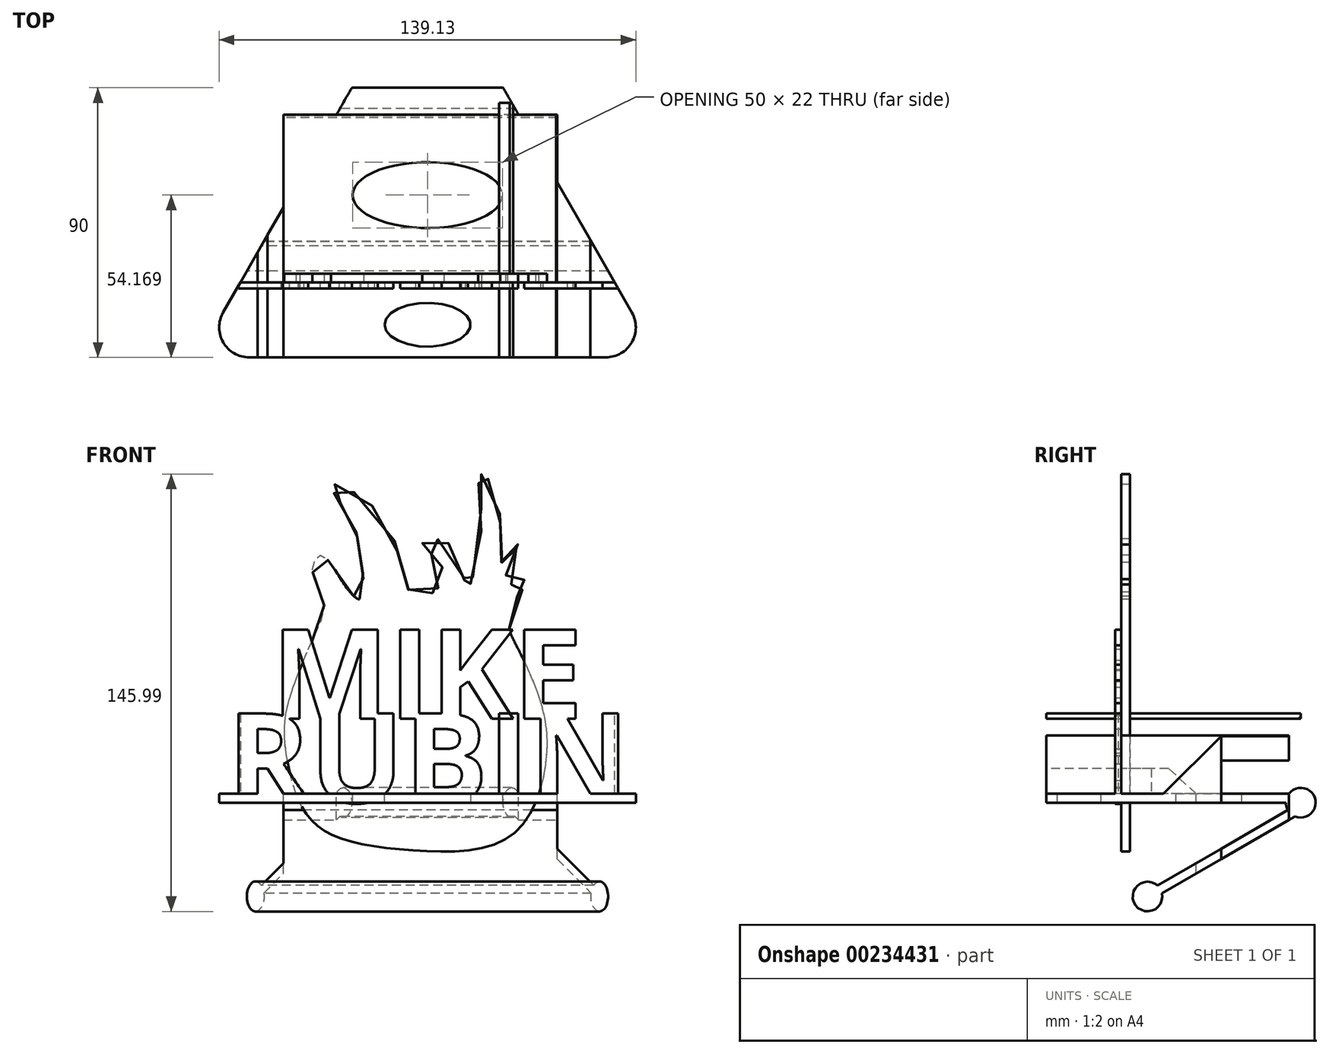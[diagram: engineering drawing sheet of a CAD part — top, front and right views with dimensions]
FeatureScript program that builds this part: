
annotation { "Feature Type Name" : "Feature", "Feature Type Description" : "" }
export const myFeature = defineFeature(function(context is Context, id is Id, definition is map)
    precondition{}
    {
        {
            var Q0;
            Q0=qCreatedBy(makeId("Front.planeOp"),FACE);
            var sketch = newSketch(context, id + "F0", { "sketchPlane" : qUnion([Q0])});
            skText(sketch, "E0", { "text": "MIKE", "fontName": "OpenSans-Bold.ttf"});
            skText(sketch, "E1", { "text": "RUBIN", "fontName": "OpenSans-Bold.ttf"});
            skLineSegment(sketch, "E2.bottom", {"start": v(-73.25, -22.3) * mm, "end": v(80.38, -22.3) * mm});
            skLineSegment(sketch, "E2.top", {"start": v(-73.25, -19.3) * mm, "end": v(80.38, -19.3) * mm});
            skLineSegment(sketch, "E2.left", {"start": v(-73.25, -22.3) * mm, "end": v(-73.25, -19.3) * mm});
            skLineSegment(sketch, "E2.right", {"start": v(80.38, -22.3) * mm, "end": v(80.38, -19.3) * mm});
            const initialGuessF0  = {"E0": [-0.0486, 0.00568, 1, 0, 0.03], "E1": [-0.06325, -0.0223, 1, 0, 0.03]};
            skSetInitialGuess(sketch, initialGuessF0);
            skSolve(sketch);
        }
        {
            var Q0;
            Q0=qCreatedBy(makeId("Front.planeOp"),FACE);
            var sketch = newSketch(context, id + "F1", { "sketchPlane" : qUnion([Q0])});
            skFitSpline(sketch, "E3", {"points": [v(0, -38.3) * mm, v(-27.15, -33.53) * mm, v(-37.73, -24.83) * mm, v(-43.2, -8.44) * mm, v(-44.05, 5.04) * mm, v(-40.46, 18.52) * mm, v(-33.64, 34.74) * mm, v(-31.08, 44.8) * mm, v(-34.83, 54.7) * mm, v(-32.1, 60.34) * mm, v(-23.57, 49.59) * mm, v(-18.62, 45.83) * mm, v(-18.45, 58.46) * mm, v(-22.89, 73.82) * mm, v(-28.52, 83.72) * mm, v(-10.94, 72.45) * mm, v(-2.92, 48.9) * mm, v(4.6, 47.37) * mm, v(8.69, 55.9) * mm, v(1.86, 64.77) * mm, v(12.78, 62.56) * mm, v(16.37, 48.05) * mm, v(21.66, 71.09) * mm, v(20.98, 87.3) * mm, v(27.12, 79.11) * mm, v(28.66, 57.95) * mm, v(33.78, 63.92) * mm, v(29.85, 50.95) * mm, v(37.02, 52.32) * mm, v(31.05, 41.9) * mm, v(33.1, 30.47) * mm, v(41.12, 11.87) * mm, v(43.16, -7.59) * mm, v(32.07, -32.85) * mm, v(0, -38.3) * mm]});
            skSolve(sketch);
        }
        {
            var Q0;
            {var subQ5=sQuery(id+"F0.wireOp",EDGE,"E0.sketch_text.stroke-0");Q0=makeQuery(id+"F0.imprint","IMPRINT",FACE,{"disambiguationData":[TD([[makeQuery(id+"F0.imprint","IMPRINT",EDGE,{"derivedFrom":subQ5}),-1.0]])]});}
            var Q1;
            {var subQ1=sQuery(id+"F0.wireOp",EDGE,"E0.sketch_text.stroke-19");Q1=makeQuery(id+"F0.imprint","IMPRINT",FACE,{"disambiguationData":[TD([[makeQuery(id+"F0.imprint","IMPRINT",EDGE,{"derivedFrom":subQ1}),-1.0]])]});}
            var Q2;
            {var subQ8=sQuery(id+"F0.wireOp",EDGE,"E0.sketch_text.stroke-24");Q2=makeQuery(id+"F0.imprint","IMPRINT",FACE,{"disambiguationData":[TD([[makeQuery(id+"F0.imprint","IMPRINT",EDGE,{"derivedFrom":subQ8}),-1.0]])]});}
            var Q3;
            {var subQ4=sQuery(id+"F0.wireOp",EDGE,"E0.sketch_text.stroke-37");Q3=makeQuery(id+"F0.imprint","IMPRINT",FACE,{"disambiguationData":[TD([[makeQuery(id+"F0.imprint","IMPRINT",EDGE,{"derivedFrom":subQ4}),-1.0]])]});}
            var Q4;
            {var subQ0=sQuery(id+"F0.wireOp",EDGE,"E0.sketch_text.stroke-35");var subQ1=sQuery(id+"F0.wireOp",EDGE,"E0.sketch_text.stroke-23");var subQ2=makeQuery(id+"F0.imprint","INTERSECT",VERTEX,{"derivedFrom":[subQ1,subQ0]});Q4=makeQuery(id+"F0.imprint","IMPRINT",FACE,{"disambiguationData":[TD([[makeQuery(id+"F0.imprint","IMPRINT",EDGE,{"disambiguationData":[TD([[subQ2,-1.0]])],"derivedFrom":subQ1}),-1.0]])]});}
            var Q5;
            {var subQ5=sQuery(id+"F0.wireOp",EDGE,"E0.sketch_text.stroke-27");Q5=makeQuery(id+"F0.imprint","IMPRINT",FACE,{"disambiguationData":[TD([[makeQuery(id+"F0.imprint","IMPRINT",EDGE,{"derivedFrom":subQ5}),-1.0]])]});}
            var Q6;
            {var subQ5=sQuery(id+"F0.wireOp",EDGE,"E1.sketch_text.stroke-70");Q6=makeQuery(id+"F0.imprint","IMPRINT",FACE,{"disambiguationData":[TD([[makeQuery(id+"F0.imprint","IMPRINT",EDGE,{"derivedFrom":subQ5}),-1.0]])]});}
            var Q7;
            {var subQ15=sQuery(id+"F0.wireOp",EDGE,"E1.sketch_text.stroke-65");Q7=makeQuery(id+"F0.imprint","IMPRINT",FACE,{"disambiguationData":[TD([[makeQuery(id+"F0.imprint","IMPRINT",EDGE,{"derivedFrom":subQ15}),-1.0]])]});}
            var Q8;
            {var subQ3=sQuery(id+"F0.wireOp",EDGE,"E0.sketch_text.stroke-35");var subQ6=sQuery(id+"F0.wireOp",EDGE,"E0.sketch_text.stroke-23");var subQ10=makeQuery(id+"F0.imprint","INTERSECT",VERTEX,{"derivedFrom":[subQ6,subQ3]});Q8=makeQuery(id+"F0.imprint","IMPRINT",FACE,{"disambiguationData":[TD([[makeQuery(id+"F0.imprint","IMPRINT",EDGE,{"disambiguationData":[TD([[subQ10,-1.0]])],"derivedFrom":subQ6}),1.0]])]});}
            var Q9;
            {var subQ12=sQuery(id+"F0.wireOp",EDGE,"E0.sketch_text.stroke-27");Q9=makeQuery(id+"F0.imprint","IMPRINT",FACE,{"disambiguationData":[TD([[makeQuery(id+"F0.imprint","IMPRINT",EDGE,{"derivedFrom":subQ12}),1.0]])]});}
            var Q10;
            {var subQ23=sQuery(id+"F0.wireOp",EDGE,"E1.sketch_text.stroke-19");Q10=makeQuery(id+"F0.imprint","IMPRINT",FACE,{"disambiguationData":[TD([[makeQuery(id+"F0.imprint","IMPRINT",EDGE,{"derivedFrom":subQ23}),-1.0]])]});}
            var Q11;
            Q11=makeQuery(id+"F0.imprint","IMPRINT",FACE,{"disambiguationData":[TD([[makeQuery(id+"F0.imprint","IMPRINT",EDGE,{"derivedFrom":sQuery(id+"F0.wireOp",EDGE,"E1.sketch_text.stroke-0")}),-1.0]])]});
            var Q12;
            {var subQ7=sQuery(id+"F0.wireOp",EDGE,"E1.sketch_text.stroke-26");Q12=makeQuery(id+"F0.imprint","IMPRINT",FACE,{"disambiguationData":[TD([[makeQuery(id+"F0.imprint","IMPRINT",EDGE,{"derivedFrom":subQ7}),-1.0]])]});}
            var Q13;
            {var subQ0=sQuery(id+"F0.wireOp",EDGE,"E0.sketch_text.stroke-12");var subQ1=sQuery(id+"F0.wireOp",EDGE,"E0.sketch_text.stroke-11");var subQ2=makeQuery(id+"F0.imprint","INTERSECT",VERTEX,{"derivedFrom":[subQ1,subQ0]});Q13=makeQuery(id+"F0.imprint","IMPRINT",FACE,{"disambiguationData":[TD([[makeQuery(id+"F0.imprint","IMPRINT",EDGE,{"disambiguationData":[TD([[subQ2,1.0]])],"derivedFrom":subQ1}),-1.0]])]});}
            var Q14;
            {var subQ0=sQuery(id+"F0.wireOp",EDGE,"E0.sketch_text.stroke-5");var subQ1=sQuery(id+"F0.wireOp",EDGE,"E0.sketch_text.stroke-4");var subQ2=makeQuery(id+"F0.imprint","INTERSECT",VERTEX,{"derivedFrom":[subQ1,subQ0]});Q14=makeQuery(id+"F0.imprint","IMPRINT",FACE,{"disambiguationData":[TD([[makeQuery(id+"F0.imprint","IMPRINT",EDGE,{"disambiguationData":[TD([[subQ2,1.0]])],"derivedFrom":subQ1}),-1.0]])]});}
            var Q15;
            {var subQ0=sQuery(id+"F0.wireOp",EDGE,"E0.sketch_text.stroke-22");var subQ1=sQuery(id+"F0.wireOp",EDGE,"E0.sketch_text.stroke-21");var subQ2=makeQuery(id+"F0.imprint","INTERSECT",VERTEX,{"derivedFrom":[subQ1,subQ0]});Q15=makeQuery(id+"F0.imprint","IMPRINT",FACE,{"disambiguationData":[TD([[makeQuery(id+"F0.imprint","IMPRINT",EDGE,{"disambiguationData":[TD([[subQ2,1.0]])],"derivedFrom":subQ1}),-1.0]])]});}
            var Q16;
            {var subQ0=sQuery(id+"F0.wireOp",EDGE,"E2.bottom");var subQ1=sQuery(id+"F0.wireOp",EDGE,"E1.sketch_text.stroke-67");var subQ2=makeQuery(id+"F0.imprint","INTERSECT",VERTEX,{"derivedFrom":[subQ1,subQ0]});Q16=makeQuery(id+"F0.imprint","IMPRINT",FACE,{"disambiguationData":[TD([[makeQuery(id+"F0.imprint","IMPRINT",EDGE,{"disambiguationData":[TD([[subQ2,1.0]])],"derivedFrom":subQ1}),-1.0]])]});}
            var Q17;
            {var subQ0=sQuery(id+"F0.wireOp",EDGE,"E2.bottom");var subQ1=sQuery(id+"F0.wireOp",EDGE,"E1.sketch_text.stroke-64");var subQ2=makeQuery(id+"F0.imprint","INTERSECT",VERTEX,{"derivedFrom":[subQ1,subQ0]});Q17=makeQuery(id+"F0.imprint","IMPRINT",FACE,{"disambiguationData":[TD([[makeQuery(id+"F0.imprint","IMPRINT",EDGE,{"disambiguationData":[TD([[subQ2,-1.0]])],"derivedFrom":subQ1}),-1.0]])]});}
            var Q18;
            {var subQ0=sQuery(id+"F0.wireOp",EDGE,"E2.bottom");var subQ1=sQuery(id+"F0.wireOp",EDGE,"E1.sketch_text.stroke-59");var subQ2=makeQuery(id+"F0.imprint","INTERSECT",VERTEX,{"derivedFrom":[subQ1,subQ0]});Q18=makeQuery(id+"F0.imprint","IMPRINT",FACE,{"disambiguationData":[TD([[makeQuery(id+"F0.imprint","IMPRINT",EDGE,{"disambiguationData":[TD([[subQ2,-1.0]])],"derivedFrom":subQ1}),-1.0]])]});}
            var Q19;
            {var subQ1=sQuery(id+"F0.wireOp",EDGE,"E1.sketch_text.stroke-43");Q19=makeQuery(id+"F0.imprint","IMPRINT",FACE,{"disambiguationData":[TD([[makeQuery(id+"F0.imprint","IMPRINT",EDGE,{"derivedFrom":subQ1}),-1.0]])]});}
            var Q20;
            {var subQ7=sQuery(id+"F0.wireOp",EDGE,"E1.sketch_text.stroke-22");var subQ8=sQuery(id+"F0.wireOp",EDGE,"E1.sketch_text.stroke-21");var subQ9=makeQuery(id+"F0.imprint","INTERSECT",VERTEX,{"derivedFrom":[subQ8,subQ7]});Q20=makeQuery(id+"F0.imprint","IMPRINT",FACE,{"disambiguationData":[TD([[makeQuery(id+"F0.imprint","IMPRINT",EDGE,{"disambiguationData":[TD([[subQ9,1.0]])],"derivedFrom":subQ8}),-1.0]])]});}
            var Q21;
            {var subQ0=sQuery(id+"F0.wireOp",EDGE,"E2.bottom");var subQ1=sQuery(id+"F0.wireOp",EDGE,"E1.sketch_text.stroke-15");var subQ2=makeQuery(id+"F0.imprint","INTERSECT",VERTEX,{"derivedFrom":[subQ1,subQ0]});Q21=makeQuery(id+"F0.imprint","IMPRINT",FACE,{"disambiguationData":[TD([[makeQuery(id+"F0.imprint","IMPRINT",EDGE,{"disambiguationData":[TD([[subQ2,1.0]])],"derivedFrom":subQ1}),-1.0]])]});}
            var Q22;
            {var subQ0=sQuery(id+"F0.wireOp",EDGE,"E2.bottom");var subQ1=sQuery(id+"F0.wireOp",EDGE,"E1.sketch_text.stroke-7");var subQ2=makeQuery(id+"F0.imprint","INTERSECT",VERTEX,{"derivedFrom":[subQ1,subQ0]});Q22=makeQuery(id+"F0.imprint","IMPRINT",FACE,{"disambiguationData":[TD([[makeQuery(id+"F0.imprint","IMPRINT",EDGE,{"disambiguationData":[TD([[subQ2,1.0]])],"derivedFrom":subQ1}),-1.0]])]});}
            var Q23;
            {var subQ0=sQuery(id+"F0.wireOp",EDGE,"E1.sketch_text.stroke-23");var subQ1=sQuery(id+"F0.wireOp",EDGE,"E1.sketch_text.stroke-22");var subQ2=makeQuery(id+"F0.imprint","INTERSECT",VERTEX,{"derivedFrom":[subQ1,subQ0]});Q23=makeQuery(id+"F0.imprint","IMPRINT",FACE,{"disambiguationData":[TD([[makeQuery(id+"F0.imprint","IMPRINT",EDGE,{"disambiguationData":[TD([[subQ2,1.0]])],"derivedFrom":subQ1}),-1.0]])]});}
            extrude(context, id + "F2", {"entities" : qUnion([Q0, Q1, Q2, Q3, Q4, Q5, Q6, Q7, Q8, Q9, Q10, Q11, Q12, Q13, Q14, Q15, Q16, Q17, Q18, Q19, Q20, Q21, Q22, Q23]), "depth" : 2 * mm});
        }
        {
            var Q0;
            Q0=makeQuery(id+"F1.imprint","IMPRINT",FACE,{"disambiguationData":[TD([[makeQuery(id+"F1.imprint","IMPRINT",EDGE,{"derivedFrom":sQuery(id+"F1.wireOp",EDGE,"E3")}),-1.0]])]});
            extrude(context, id + "F3", {"entities" : qUnion([Q0]), "operationType" : NewBodyOperationType.ADD, "oppositeDirection" : true, "depth" : 3 * mm});
        }
        {
            var Q0;
            {var subQ5=sQuery(id+"F0.wireOp",EDGE,"E2.right");Q0=makeQuery(id+"F0.imprint","IMPRINT",FACE,{"disambiguationData":[TD([[makeQuery(id+"F0.imprint","IMPRINT",EDGE,{"derivedFrom":subQ5}),1.0]])]});}
            var Q1;
            {var subQ0=sQuery(id+"F0.wireOp",EDGE,"E2.bottom");var subQ1=sQuery(id+"F0.wireOp",EDGE,"E1.sketch_text.stroke-64");var subQ2=makeQuery(id+"F0.imprint","INTERSECT",VERTEX,{"derivedFrom":[subQ1,subQ0]});Q1=makeQuery(id+"F0.imprint","IMPRINT",FACE,{"disambiguationData":[TD([[makeQuery(id+"F0.imprint","IMPRINT",EDGE,{"disambiguationData":[TD([[subQ2,-1.0]])],"derivedFrom":subQ1}),-1.0]])]});}
            var Q2;
            {var subQ0=sQuery(id+"F0.wireOp",EDGE,"E2.bottom");var subQ1=sQuery(id+"F0.wireOp",EDGE,"E1.sketch_text.stroke-64");var subQ2=makeQuery(id+"F0.imprint","INTERSECT",VERTEX,{"derivedFrom":[subQ1,subQ0]});Q2=makeQuery(id+"F0.imprint","IMPRINT",FACE,{"disambiguationData":[TD([[makeQuery(id+"F0.imprint","IMPRINT",EDGE,{"disambiguationData":[TD([[subQ2,-1.0]])],"derivedFrom":subQ1}),1.0]])]});}
            var Q3;
            {var subQ0=sQuery(id+"F0.wireOp",EDGE,"E2.bottom");var subQ1=sQuery(id+"F0.wireOp",EDGE,"E1.sketch_text.stroke-67");var subQ2=makeQuery(id+"F0.imprint","INTERSECT",VERTEX,{"derivedFrom":[subQ1,subQ0]});Q3=makeQuery(id+"F0.imprint","IMPRINT",FACE,{"disambiguationData":[TD([[makeQuery(id+"F0.imprint","IMPRINT",EDGE,{"disambiguationData":[TD([[subQ2,1.0]])],"derivedFrom":subQ1}),-1.0]])]});}
            var Q4;
            {var subQ0=sQuery(id+"F0.wireOp",EDGE,"E2.bottom");var subQ1=sQuery(id+"F0.wireOp",EDGE,"E1.sketch_text.stroke-61");var subQ2=makeQuery(id+"F0.imprint","INTERSECT",VERTEX,{"derivedFrom":[subQ1,subQ0]});Q4=makeQuery(id+"F0.imprint","IMPRINT",FACE,{"disambiguationData":[TD([[makeQuery(id+"F0.imprint","IMPRINT",EDGE,{"disambiguationData":[TD([[subQ2,1.0]])],"derivedFrom":subQ1}),1.0]])]});}
            var Q5;
            {var subQ0=sQuery(id+"F0.wireOp",EDGE,"E2.bottom");var subQ1=sQuery(id+"F0.wireOp",EDGE,"E1.sketch_text.stroke-59");var subQ2=makeQuery(id+"F0.imprint","INTERSECT",VERTEX,{"derivedFrom":[subQ1,subQ0]});Q5=makeQuery(id+"F0.imprint","IMPRINT",FACE,{"disambiguationData":[TD([[makeQuery(id+"F0.imprint","IMPRINT",EDGE,{"disambiguationData":[TD([[subQ2,-1.0]])],"derivedFrom":subQ1}),-1.0]])]});}
            var Q6;
            {var subQ1=sQuery(id+"F0.wireOp",EDGE,"E1.sketch_text.stroke-43");Q6=makeQuery(id+"F0.imprint","IMPRINT",FACE,{"disambiguationData":[TD([[makeQuery(id+"F0.imprint","IMPRINT",EDGE,{"derivedFrom":subQ1}),1.0]])]});}
            var Q7;
            {var subQ1=sQuery(id+"F0.wireOp",EDGE,"E1.sketch_text.stroke-43");Q7=makeQuery(id+"F0.imprint","IMPRINT",FACE,{"disambiguationData":[TD([[makeQuery(id+"F0.imprint","IMPRINT",EDGE,{"derivedFrom":subQ1}),-1.0]])]});}
            var Q8;
            {var subQ3=sQuery(id+"F0.wireOp",EDGE,"E1.sketch_text.stroke-22");var subQ5=sQuery(id+"F0.wireOp",EDGE,"E1.sketch_text.stroke-21");var subQ6=makeQuery(id+"F0.imprint","INTERSECT",VERTEX,{"derivedFrom":[subQ5,subQ3]});Q8=makeQuery(id+"F0.imprint","IMPRINT",FACE,{"disambiguationData":[TD([[makeQuery(id+"F0.imprint","IMPRINT",EDGE,{"disambiguationData":[TD([[subQ6,1.0]])],"derivedFrom":subQ5}),1.0]])]});}
            var Q9;
            {var subQ5=sQuery(id+"F0.wireOp",EDGE,"E2.left");Q9=makeQuery(id+"F0.imprint","IMPRINT",FACE,{"disambiguationData":[TD([[makeQuery(id+"F0.imprint","IMPRINT",EDGE,{"derivedFrom":subQ5}),-1.0]])]});}
            var Q10;
            {var subQ0=sQuery(id+"F0.wireOp",EDGE,"E2.bottom");var subQ1=sQuery(id+"F0.wireOp",EDGE,"E1.sketch_text.stroke-7");var subQ2=makeQuery(id+"F0.imprint","INTERSECT",VERTEX,{"derivedFrom":[subQ1,subQ0]});Q10=makeQuery(id+"F0.imprint","IMPRINT",FACE,{"disambiguationData":[TD([[makeQuery(id+"F0.imprint","IMPRINT",EDGE,{"disambiguationData":[TD([[subQ2,1.0]])],"derivedFrom":subQ1}),-1.0]])]});}
            var Q11;
            {var subQ0=sQuery(id+"F0.wireOp",EDGE,"E2.bottom");var subQ1=sQuery(id+"F0.wireOp",EDGE,"E1.sketch_text.stroke-7");var subQ2=makeQuery(id+"F0.imprint","INTERSECT",VERTEX,{"derivedFrom":[subQ1,subQ0]});Q11=makeQuery(id+"F0.imprint","IMPRINT",FACE,{"disambiguationData":[TD([[makeQuery(id+"F0.imprint","IMPRINT",EDGE,{"disambiguationData":[TD([[subQ2,1.0]])],"derivedFrom":subQ1}),1.0]])]});}
            var Q12;
            {var subQ0=sQuery(id+"F0.wireOp",EDGE,"E2.bottom");var subQ1=sQuery(id+"F0.wireOp",EDGE,"E1.sketch_text.stroke-15");var subQ2=makeQuery(id+"F0.imprint","INTERSECT",VERTEX,{"derivedFrom":[subQ1,subQ0]});Q12=makeQuery(id+"F0.imprint","IMPRINT",FACE,{"disambiguationData":[TD([[makeQuery(id+"F0.imprint","IMPRINT",EDGE,{"disambiguationData":[TD([[subQ2,1.0]])],"derivedFrom":subQ1}),-1.0]])]});}
            var Q13;
            {var subQ0=sQuery(id+"F0.wireOp",EDGE,"E2.bottom");var subQ1=sQuery(id+"F0.wireOp",EDGE,"E1.sketch_text.stroke-15");var subQ2=makeQuery(id+"F0.imprint","INTERSECT",VERTEX,{"derivedFrom":[subQ1,subQ0]});Q13=makeQuery(id+"F0.imprint","IMPRINT",FACE,{"disambiguationData":[TD([[makeQuery(id+"F0.imprint","IMPRINT",EDGE,{"disambiguationData":[TD([[subQ2,1.0]])],"derivedFrom":subQ1}),1.0]])]});}
            var Q14;
            {var subQ7=sQuery(id+"F0.wireOp",EDGE,"E1.sketch_text.stroke-22");var subQ8=sQuery(id+"F0.wireOp",EDGE,"E1.sketch_text.stroke-21");var subQ9=makeQuery(id+"F0.imprint","INTERSECT",VERTEX,{"derivedFrom":[subQ8,subQ7]});Q14=makeQuery(id+"F0.imprint","IMPRINT",FACE,{"disambiguationData":[TD([[makeQuery(id+"F0.imprint","IMPRINT",EDGE,{"disambiguationData":[TD([[subQ9,1.0]])],"derivedFrom":subQ8}),-1.0]])]});}
            extrude(context, id + "F4", {"entities" : qUnion([Q0, Q1, Q2, Q3, Q4, Q5, Q6, Q7, Q8, Q9, Q10, Q11, Q12, Q13, Q14]), "operationType" : NewBodyOperationType.ADD, "oppositeDirection" : true, "depth" : 60 * mm, "hasSecondDirection" : true, "secondDirectionOppositeDirection" : false, "secondDirectionDepth" : 25 * mm});
        }
        {
            var Q0;
            Q0=makeQuery(id+"F4.opExtrude","SWEPT_FACE",FACE,{"disambiguationData":[OSD([sQuery(id+"F0.wireOp",EDGE,"E2.left")])]});
            var sketch = newSketch(context, id + "F5", { "sketchPlane" : qUnion([Q0])});
            skLineSegment(sketch, "E4", {"start": v(-60, -22.3) * mm, "end": v(-8.04, -52.3) * mm});
            skLineSegment(sketch, "E5", {"start": v(-60, -22.3) * mm, "end": v(-61.5, -24.9) * mm});
            skLineSegment(sketch, "E6", {"start": v(-61.5, -24.9) * mm, "end": v(-9.54, -54.9) * mm});
            skLineSegment(sketch, "E7", {"start": v(-9.54, -54.9) * mm, "end": v(-8.04, -52.3) * mm});
            skCircle(sketch, "E8", {"center": v(-60, -22.3) * mm, "radius": 5 * mm});
            skCircle(sketch, "E9", {"center": v(-8.79, -53.6) * mm, "radius": 5 * mm});
            skSolve(sketch);
        }
        {
            var Q0;
            {var subQ7=sQuery(id+"F5.wireOp",EDGE,"E5");Q0=makeQuery(id+"F5.imprint","IMPRINT",FACE,{"disambiguationData":[TD([[makeQuery(id+"F5.imprint","IMPRINT",EDGE,{"derivedFrom":subQ7}),-1.0]])]});}
            var Q1;
            {var subQ0=sQuery(id+"F5.wireOp",EDGE,"E4");var subQ4=sQuery(id+"F5.wireOp",EDGE,"E8");var subQ5=makeQuery(id+"F5.imprint","INTERSECT",VERTEX,{"derivedFrom":[subQ0,subQ4]});Q1=makeQuery(id+"F5.imprint","IMPRINT",FACE,{"disambiguationData":[TD([[makeQuery(id+"F5.imprint","IMPRINT",EDGE,{"disambiguationData":[TD([[subQ5,-1.0]])],"derivedFrom":subQ4}),1.0]])]});}
            var Q2;
            {var subQ0=sQuery(id+"F5.wireOp",EDGE,"E5");Q2=makeQuery(id+"F5.imprint","IMPRINT",FACE,{"disambiguationData":[TD([[makeQuery(id+"F5.imprint","IMPRINT",EDGE,{"derivedFrom":subQ0}),1.0]])]});}
            var Q3;
            {var subQ0=sQuery(id+"F5.wireOp",EDGE,"E8");var subQ1=sQuery(id+"F5.wireOp",EDGE,"E4");var subQ2=makeQuery(id+"F5.imprint","INTERSECT",VERTEX,{"derivedFrom":[subQ1,subQ0]});Q3=makeQuery(id+"F5.imprint","IMPRINT",FACE,{"disambiguationData":[TD([[makeQuery(id+"F5.imprint","IMPRINT",EDGE,{"disambiguationData":[TD([[subQ2,-1.0]])],"derivedFrom":subQ1}),-1.0]])]});}
            var Q4;
            {var subQ0=sQuery(id+"F5.wireOp",EDGE,"E7");Q4=makeQuery(id+"F5.imprint","IMPRINT",FACE,{"disambiguationData":[TD([[makeQuery(id+"F5.imprint","IMPRINT",EDGE,{"derivedFrom":subQ0}),1.0]])]});}
            var Q5;
            {var subQ0=sQuery(id+"F5.wireOp",EDGE,"E7");Q5=makeQuery(id+"F5.imprint","IMPRINT",FACE,{"disambiguationData":[TD([[makeQuery(id+"F5.imprint","IMPRINT",EDGE,{"derivedFrom":subQ0}),-1.0]])]});}
            var Q6;
            Q6=makeQuery(id+"F4.opExtrude","SWEPT_FACE",FACE,{"disambiguationData":[OSD([sQuery(id+"F0.wireOp",EDGE,"E2.right")])]});
            extrude(context, id + "F6", {"entities" : qUnion([Q0, Q1, Q2, Q3, Q4, Q5]), "operationType" : NewBodyOperationType.ADD, "endBound" : BoundingType.UP_TO_SURFACE, "oppositeDirection" : true, "endBoundEntityFace" : qUnion([Q6]), "depth" : 25 * mm});
        }
        {
            var Q0;
            Q0=makeQuery(id+"F4.opExtrude","SWEPT_FACE",FACE,{"disambiguationData":[OSD([sQuery(id+"F0.wireOp",EDGE,"E2.top")])]});
            var sketch = newSketch(context, id + "F7", { "sketchPlane" : qUnion([Q0])});
            skLineSegment(sketch, "E10", {"start": v(80.38, -25) * mm, "end": v(28.56, 65.48) * mm});
            skLineSegment(sketch, "E11", {"start": v(28.56, 65.48) * mm, "end": v(-21.44, 65.48) * mm});
            skLineSegment(sketch, "E12", {"start": v(-21.44, 65.48) * mm, "end": v(-73.25, -25) * mm});
            skLineSegment(sketch, "E13.bottom", {"start": v(80.38, -25) * mm, "end": v(-73.25, -25) * mm});
            skLineSegment(sketch, "E13.top", {"start": v(80.38, 65.48) * mm, "end": v(-73.25, 65.48) * mm});
            skLineSegment(sketch, "E13.left", {"start": v(80.38, -25) * mm, "end": v(80.38, 65.48) * mm});
            skLineSegment(sketch, "E13.right", {"start": v(-73.25, -25) * mm, "end": v(-73.25, 65.48) * mm});
            skSolve(sketch);
        }
        {
            var Q0;
            {var subQ6=sQuery(id+"F7.wireOp",EDGE,"E10");var subQ9=sQuery(id+"F7.wireOp",EDGE,"E13.left");var subQ10=makeQuery(id+"F7.imprint","INTERSECT",VERTEX,{"derivedFrom":[subQ6,sQuery(id+"F7.wireOp",EDGE,"E13.bottom"),subQ9]});Q0=makeQuery(id+"F7.imprint","IMPRINT",FACE,{"disambiguationData":[TD([[makeQuery(id+"F7.imprint","IMPRINT",EDGE,{"disambiguationData":[TD([[subQ10,-1.0]])],"derivedFrom":subQ6}),-1.0]])]});}
            var Q1;
            {var subQ0=sQuery(id+"F7.wireOp",EDGE,"E13.top");var subQ1=sQuery(id+"F7.wireOp",EDGE,"E10");var subQ2=makeQuery(id+"F7.imprint","INTERSECT",VERTEX,{"derivedFrom":[subQ1,subQ0]});Q1=makeQuery(id+"F7.imprint","IMPRINT",FACE,{"disambiguationData":[TD([[makeQuery(id+"F7.imprint","IMPRINT",EDGE,{"disambiguationData":[TD([[subQ2,1.0]])],"derivedFrom":subQ0}),1.0]])]});}
            var Q2;
            {var subQ0=sQuery(id+"F7.wireOp",EDGE,"E13.top");var subQ1=sQuery(id+"F7.wireOp",EDGE,"E12");var subQ2=makeQuery(id+"F7.imprint","INTERSECT",VERTEX,{"derivedFrom":[subQ1,subQ0]});Q2=makeQuery(id+"F7.imprint","IMPRINT",FACE,{"disambiguationData":[TD([[makeQuery(id+"F7.imprint","IMPRINT",EDGE,{"disambiguationData":[TD([[subQ2,-1.0]])],"derivedFrom":subQ0}),1.0]])]});}
            var Q3;
            {var subQ6=sQuery(id+"F7.wireOp",EDGE,"E12");var subQ8=sQuery(id+"F7.wireOp",EDGE,"E13.right");var subQ9=makeQuery(id+"F7.imprint","INTERSECT",VERTEX,{"derivedFrom":[subQ6,sQuery(id+"F7.wireOp",EDGE,"E13.bottom"),subQ8]});Q3=makeQuery(id+"F7.imprint","IMPRINT",FACE,{"disambiguationData":[TD([[makeQuery(id+"F7.imprint","IMPRINT",EDGE,{"disambiguationData":[TD([[subQ9,1.0]])],"derivedFrom":subQ6}),-1.0]])]});}
            extrude(context, id + "F8", {"entities" : qUnion([Q0, Q1, Q2, Q3]), "operationType" : NewBodyOperationType.REMOVE, "endBound" : BoundingType.SYMMETRIC, "oppositeDirection" : true, "depth" : 100 * mm});
        }
        {
            var Q0;
            Q0=makeQuery(id+"F8.boolean.opBoolean","MERGE",EDGE,{"derivedFrom":[makeQuery(id+"F4.opExtrude","CAP_EDGE",EDGE,{"disambiguationData":[OSD([sQuery(id+"F0.wireOp",EDGE,"E2.left")])],"isStart":true}),makeQuery(id+"F8.opExtrude","SWEPT_EDGE",EDGE,{"disambiguationData":[OSD([sQuery(id+"F7.wireOp",EDGE,"E12"),sQuery(id+"F7.wireOp",EDGE,"E13.bottom"),sQuery(id+"F7.wireOp",EDGE,"E13.right")])]})]});
            var Q1;
            Q1=makeQuery(id+"F8.boolean.opBoolean","MERGE",EDGE,{"derivedFrom":[makeQuery(id+"F4.opExtrude","CAP_EDGE",EDGE,{"disambiguationData":[OSD([sQuery(id+"F0.wireOp",EDGE,"E2.right")])],"isStart":true}),makeQuery(id+"F8.opExtrude","SWEPT_EDGE",EDGE,{"disambiguationData":[OSD([sQuery(id+"F7.wireOp",EDGE,"E10"),sQuery(id+"F7.wireOp",EDGE,"E13.bottom"),sQuery(id+"F7.wireOp",EDGE,"E13.left")])]})]});
            fillet(context, id + "F9", {"entities" : qUnion([Q0, Q1]), "radius" : 10 * mm, "tangentPropagation" : true, "allowEdgeOverflow" : false});
        }
        {
            var Q0;
            Q0=makeQuery(id+"F4.opExtrude","SWEPT_FACE",FACE,{"disambiguationData":[OSD([sQuery(id+"F0.wireOp",EDGE,"E2.top")])]});
            var sketch = newSketch(context, id + "F10", { "sketchPlane" : qUnion([Q0])});
            skEllipse(sketch, "E14", {"center": v(3.56, -14.12) * mm, "majorRadius": 14.35 * mm, "minorRadius": 7.3 * mm, "majorAxis": v(-1, 0)});
            skPoint(sketch, "E14.centerSnap0", {"position": v(3.56, -25) * mm});
            skEllipse(sketch, "E15", {"center": v(3.56, 29.17) * mm, "majorRadius": 25 * mm, "minorRadius": 11 * mm, "majorAxis": v(-1, 0)});
            skPoint(sketch, "E15.centerSnap0", {"position": v(3.56, -6.82) * mm});
            skSolve(sketch);
        }
        {
            var Q0;
            Q0 = qSketchRegion(id + "F10", true);
            var Q1;
            {var subQ0=sQuery(id+"F0.wireOp",EDGE,"E2.bottom");Q1=makeQuery(id+"F4.boolean.opBoolean","MERGE",FACE,{"derivedFrom":[makeQuery(id+"F2.opExtrude","SWEPT_FACE",FACE,{"disambiguationData":[OSD([subQ0]),TDD([makeQuery(id+"F0.imprint","IMPRINT",EDGE,{"disambiguationData":[TD([[makeQuery(id+"F0.imprint","INTERSECT",VERTEX,{"derivedFrom":[sQuery(id+"F0.wireOp",EDGE,"E1.sketch_text.stroke-7"),subQ0]}),1.0]])],"derivedFrom":subQ0})])]}),makeQuery(id+"F2.opExtrude","SWEPT_FACE",FACE,{"disambiguationData":[OSD([subQ0]),TDD([makeQuery(id+"F0.imprint","IMPRINT",EDGE,{"disambiguationData":[TD([[makeQuery(id+"F0.imprint","INTERSECT",VERTEX,{"derivedFrom":[sQuery(id+"F0.wireOp",EDGE,"E1.sketch_text.stroke-15"),subQ0]}),1.0]])],"derivedFrom":subQ0})])]}),makeQuery(id+"F2.opExtrude","SWEPT_FACE",FACE,{"disambiguationData":[OSD([subQ0]),TDD([makeQuery(id+"F0.imprint","IMPRINT",EDGE,{"disambiguationData":[TD([[makeQuery(id+"F0.imprint","INTERSECT",VERTEX,{"derivedFrom":[sQuery(id+"F0.wireOp",EDGE,"E1.sketch_text.stroke-43"),subQ0]}),1.0]])],"derivedFrom":subQ0})])]}),makeQuery(id+"F2.opExtrude","SWEPT_FACE",FACE,{"disambiguationData":[OSD([subQ0]),TDD([makeQuery(id+"F0.imprint","IMPRINT",EDGE,{"disambiguationData":[TD([[makeQuery(id+"F0.imprint","INTERSECT",VERTEX,{"derivedFrom":[sQuery(id+"F0.wireOp",EDGE,"E1.sketch_text.stroke-59"),subQ0]}),-1.0]])],"derivedFrom":subQ0})])]}),makeQuery(id+"F2.opExtrude","SWEPT_FACE",FACE,{"disambiguationData":[OSD([subQ0]),TDD([makeQuery(id+"F0.imprint","IMPRINT",EDGE,{"disambiguationData":[TD([[makeQuery(id+"F0.imprint","INTERSECT",VERTEX,{"derivedFrom":[sQuery(id+"F0.wireOp",EDGE,"E1.sketch_text.stroke-67"),subQ0]}),1.0]])],"derivedFrom":subQ0})])]}),makeQuery(id+"F2.opExtrude","SWEPT_FACE",FACE,{"disambiguationData":[OSD([subQ0]),TDD([makeQuery(id+"F0.imprint","IMPRINT",EDGE,{"disambiguationData":[TD([[makeQuery(id+"F0.imprint","INTERSECT",VERTEX,{"derivedFrom":[sQuery(id+"F0.wireOp",EDGE,"E1.sketch_text.stroke-64"),subQ0]}),-1.0]])],"derivedFrom":subQ0})])]}),makeQuery(id+"F4.opExtrude","SWEPT_FACE",FACE,{"disambiguationData":[OSD([subQ0])]})]});}
            extrude(context, id + "F11", {"entities" : qUnion([Q0]), "operationType" : NewBodyOperationType.REMOVE, "endBound" : BoundingType.UP_TO_SURFACE, "oppositeDirection" : true, "endBoundEntityFace" : qUnion([Q1]), "depth" : 25 * mm});
        }
    });
